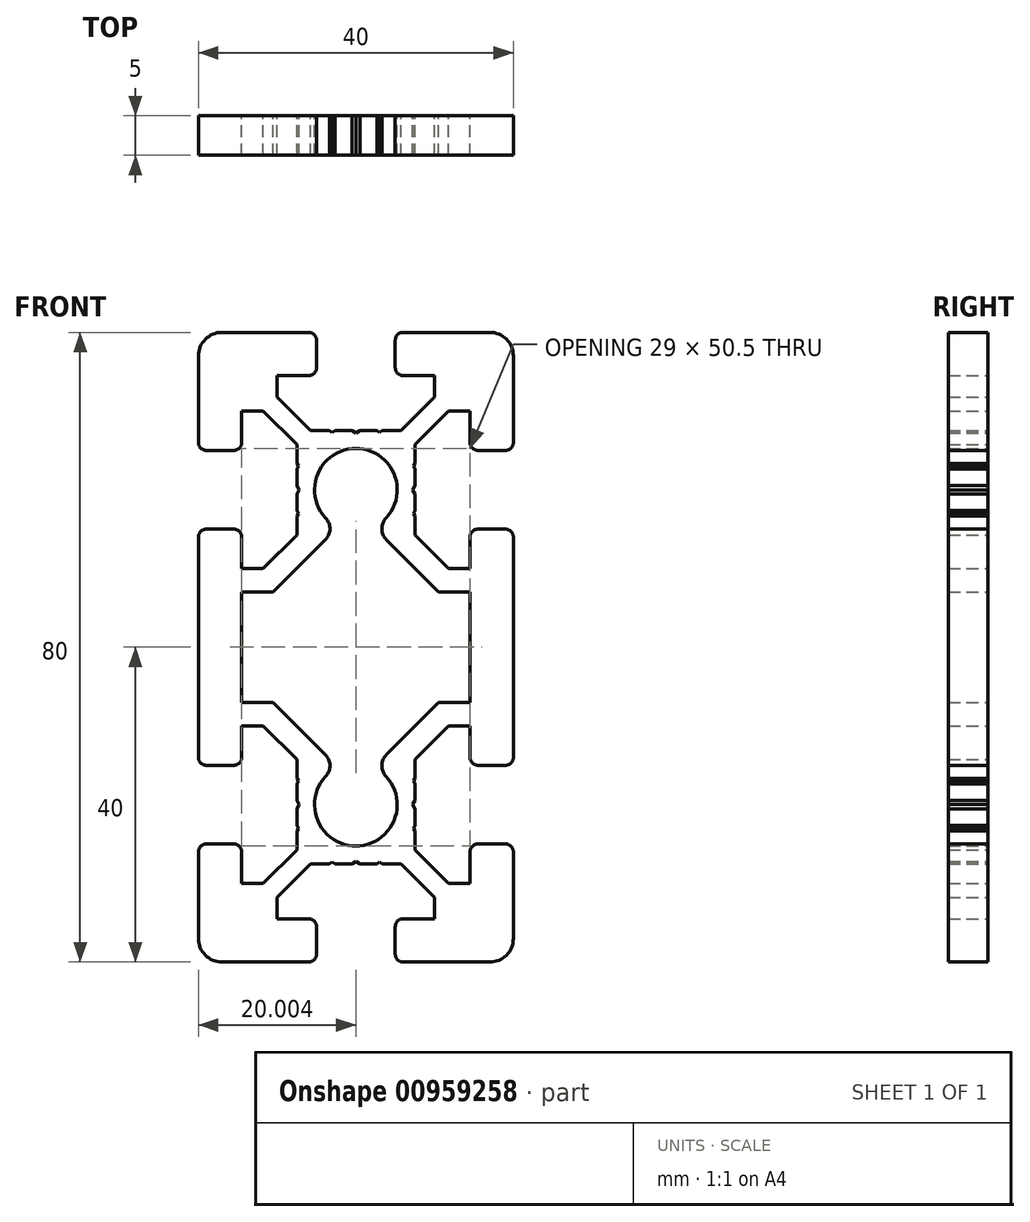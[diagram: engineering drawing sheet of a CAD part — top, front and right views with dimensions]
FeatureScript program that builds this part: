
annotation { "Feature Type Name" : "Feature", "Feature Type Description" : "" }
export const myFeature = defineFeature(function(context is Context, id is Id, definition is map)
    precondition{}
    {
        {
            assignVariable(context, id + "F0", {"name" : "length", "anyValue" : 5});
        }
        {
            var Q0;
            Q0=qCreatedBy(makeId("Front.planeOp"),FACE);
            var sketch = newSketch(context, id + "F1", { "sketchPlane" : qUnion([Q0])});
            skLineSegment(sketch, "E0", {"start": v(-9.74, 19.75) * mm, "end": v(1.29, 19.75) * mm});
            skLineSegment(sketch, "E1", {"start": v(-4.23, 14.24) * mm, "end": v(-4.23, 25.26) * mm});
            skLineSegment(sketch, "E2", {"start": v(-9.74, -20.25) * mm, "end": v(1.29, -20.25) * mm});
            skLineSegment(sketch, "E3", {"start": v(-4.23, -25.76) * mm, "end": v(-4.23, -14.74) * mm});
            skArc(sketch, "E4", {"start": v(-23.23, -25.25) * mm, "mid": v(-23.93, -25.54) * mm, "end": v(-24.23, -26.25) * mm});
            skLineSegment(sketch, "E5", {"start": v(-24.23, -26.25) * mm, "end": v(-24.23, -37.25) * mm});
            skArc(sketch, "E6", {"start": v(-24.23, -37.25) * mm, "mid": v(-23.35, -39.37) * mm, "end": v(-21.23, -40.25) * mm});
            skLineSegment(sketch, "E7", {"start": v(-21.23, -40.25) * mm, "end": v(-10.23, -40.25) * mm});
            skArc(sketch, "E8", {"start": v(-10.23, -40.25) * mm, "mid": v(-9.52, -39.96) * mm, "end": v(-9.23, -39.25) * mm});
            skLineSegment(sketch, "E9", {"start": v(-9.23, -39.25) * mm, "end": v(-9.23, -35.75) * mm});
            skArc(sketch, "E10", {"start": v(-9.23, -35.75) * mm, "mid": v(-9.52, -35.04) * mm, "end": v(-10.23, -34.75) * mm});
            skLineSegment(sketch, "E11", {"start": v(-10.23, -34.75) * mm, "end": v(-14.23, -34.75) * mm});
            skLineSegment(sketch, "E12", {"start": v(-14.23, -34.75) * mm, "end": v(-14.23, -32.02) * mm});
            skLineSegment(sketch, "E13", {"start": v(-14.23, -32.02) * mm, "end": v(-9.96, -27.75) * mm});
            skLineSegment(sketch, "E14", {"start": v(-9.96, -27.75) * mm, "end": v(-7.57, -27.75) * mm});
            skLineSegment(sketch, "E15", {"start": v(-7.57, -27.75) * mm, "end": v(-7.23, -27.55) * mm});
            skLineSegment(sketch, "E16", {"start": v(-7.23, -27.55) * mm, "end": v(-6.88, -27.75) * mm});
            skLineSegment(sketch, "E17", {"start": v(-6.88, -27.75) * mm, "end": v(-4.75, -27.75) * mm});
            skLineSegment(sketch, "E18", {"start": v(-4.75, -27.75) * mm, "end": v(-4.23, -27.45) * mm});
            skLineSegment(sketch, "E19", {"start": v(-4.23, -27.45) * mm, "end": v(-3.7, -27.75) * mm});
            skLineSegment(sketch, "E20", {"start": v(-3.7, -27.75) * mm, "end": v(-1.57, -27.75) * mm});
            skLineSegment(sketch, "E21", {"start": v(-1.57, -27.75) * mm, "end": v(-1.23, -27.55) * mm});
            skLineSegment(sketch, "E22", {"start": v(-1.23, -27.55) * mm, "end": v(-0.88, -27.75) * mm});
            skLineSegment(sketch, "E23", {"start": v(-0.88, -27.75) * mm, "end": v(1.5, -27.75) * mm});
            skLineSegment(sketch, "E24", {"start": v(1.5, -27.75) * mm, "end": v(5.77, -32.02) * mm});
            skLineSegment(sketch, "E25", {"start": v(5.77, -32.02) * mm, "end": v(5.77, -34.75) * mm});
            skLineSegment(sketch, "E26", {"start": v(5.77, -34.75) * mm, "end": v(1.77, -34.75) * mm});
            skArc(sketch, "E27", {"start": v(1.77, -34.75) * mm, "mid": v(1.07, -35.04) * mm, "end": v(0.77, -35.75) * mm});
            skLineSegment(sketch, "E28", {"start": v(0.77, -35.75) * mm, "end": v(0.77, -39.25) * mm});
            skArc(sketch, "E29", {"start": v(0.77, -39.25) * mm, "mid": v(1.07, -39.96) * mm, "end": v(1.77, -40.25) * mm});
            skLineSegment(sketch, "E30", {"start": v(1.77, -40.25) * mm, "end": v(12.77, -40.25) * mm});
            skArc(sketch, "E31", {"start": v(12.77, -40.25) * mm, "mid": v(14.9, -39.37) * mm, "end": v(15.77, -37.25) * mm});
            skLineSegment(sketch, "E32", {"start": v(15.77, -37.25) * mm, "end": v(15.77, -26.25) * mm});
            skArc(sketch, "E33", {"start": v(15.77, -26.25) * mm, "mid": v(15.48, -25.54) * mm, "end": v(14.77, -25.25) * mm});
            skLineSegment(sketch, "E34", {"start": v(14.77, -25.25) * mm, "end": v(11.27, -25.25) * mm});
            skArc(sketch, "E35", {"start": v(11.27, -25.25) * mm, "mid": v(10.57, -25.54) * mm, "end": v(10.27, -26.25) * mm});
            skLineSegment(sketch, "E36", {"start": v(10.27, -26.25) * mm, "end": v(10.27, -30.25) * mm});
            skLineSegment(sketch, "E37", {"start": v(10.27, -30.25) * mm, "end": v(7.54, -30.25) * mm});
            skLineSegment(sketch, "E38", {"start": v(7.54, -30.25) * mm, "end": v(3.27, -25.98) * mm});
            skLineSegment(sketch, "E39", {"start": v(3.27, -25.98) * mm, "end": v(3.27, -23.6) * mm});
            skLineSegment(sketch, "E40", {"start": v(3.27, -23.6) * mm, "end": v(3.07, -23.25) * mm});
            skLineSegment(sketch, "E41", {"start": v(3.07, -23.25) * mm, "end": v(3.27, -22.9) * mm});
            skLineSegment(sketch, "E42", {"start": v(3.27, -22.9) * mm, "end": v(3.27, -20.77) * mm});
            skLineSegment(sketch, "E43", {"start": v(3.27, -20.77) * mm, "end": v(2.97, -20.25) * mm});
            skLineSegment(sketch, "E44", {"start": v(2.97, -20.25) * mm, "end": v(3.27, -19.73) * mm});
            skLineSegment(sketch, "E45", {"start": v(3.27, -19.73) * mm, "end": v(3.27, -17.6) * mm});
            skLineSegment(sketch, "E46", {"start": v(3.27, -17.6) * mm, "end": v(3.07, -17.25) * mm});
            skLineSegment(sketch, "E47", {"start": v(3.07, -17.25) * mm, "end": v(3.27, -16.9) * mm});
            skLineSegment(sketch, "E48", {"start": v(3.27, -16.9) * mm, "end": v(3.27, -14.52) * mm});
            skLineSegment(sketch, "E49", {"start": v(3.27, -14.52) * mm, "end": v(7.54, -10.25) * mm});
            skLineSegment(sketch, "E50", {"start": v(7.54, -10.25) * mm, "end": v(10.27, -10.25) * mm});
            skLineSegment(sketch, "E51", {"start": v(10.27, -10.25) * mm, "end": v(10.27, -14.25) * mm});
            skArc(sketch, "E52", {"start": v(10.27, -14.25) * mm, "mid": v(10.57, -14.96) * mm, "end": v(11.27, -15.25) * mm});
            skLineSegment(sketch, "E53", {"start": v(11.27, -15.25) * mm, "end": v(14.77, -15.25) * mm});
            skArc(sketch, "E54", {"start": v(14.77, -15.25) * mm, "mid": v(15.48, -14.96) * mm, "end": v(15.77, -14.25) * mm});
            skLineSegment(sketch, "E55", {"start": v(15.77, -14.25) * mm, "end": v(15.77, 13.75) * mm});
            skArc(sketch, "E56", {"start": v(15.77, 13.75) * mm, "mid": v(15.48, 14.46) * mm, "end": v(14.77, 14.75) * mm});
            skLineSegment(sketch, "E57", {"start": v(14.77, 14.75) * mm, "end": v(11.27, 14.75) * mm});
            skArc(sketch, "E58", {"start": v(11.27, 14.75) * mm, "mid": v(10.57, 14.46) * mm, "end": v(10.27, 13.75) * mm});
            skLineSegment(sketch, "E59", {"start": v(10.27, 13.75) * mm, "end": v(10.27, 9.75) * mm});
            skLineSegment(sketch, "E60", {"start": v(10.27, 9.75) * mm, "end": v(7.54, 9.75) * mm});
            skLineSegment(sketch, "E61", {"start": v(7.54, 9.75) * mm, "end": v(3.27, 14.02) * mm});
            skLineSegment(sketch, "E62", {"start": v(3.27, 14.02) * mm, "end": v(3.27, 16.4) * mm});
            skLineSegment(sketch, "E63", {"start": v(3.27, 16.4) * mm, "end": v(3.07, 16.75) * mm});
            skLineSegment(sketch, "E64", {"start": v(3.07, 16.75) * mm, "end": v(3.27, 17.1) * mm});
            skLineSegment(sketch, "E65", {"start": v(3.27, 17.1) * mm, "end": v(3.27, 19.23) * mm});
            skLineSegment(sketch, "E66", {"start": v(3.27, 19.23) * mm, "end": v(2.97, 19.75) * mm});
            skLineSegment(sketch, "E67", {"start": v(2.97, 19.75) * mm, "end": v(3.27, 20.27) * mm});
            skLineSegment(sketch, "E68", {"start": v(3.27, 20.27) * mm, "end": v(3.27, 22.4) * mm});
            skLineSegment(sketch, "E69", {"start": v(3.27, 22.4) * mm, "end": v(3.07, 22.75) * mm});
            skLineSegment(sketch, "E70", {"start": v(3.07, 22.75) * mm, "end": v(3.27, 23.1) * mm});
            skLineSegment(sketch, "E71", {"start": v(3.27, 23.1) * mm, "end": v(3.27, 25.48) * mm});
            skLineSegment(sketch, "E72", {"start": v(3.27, 25.48) * mm, "end": v(7.54, 29.75) * mm});
            skLineSegment(sketch, "E73", {"start": v(7.54, 29.75) * mm, "end": v(10.27, 29.75) * mm});
            skLineSegment(sketch, "E74", {"start": v(10.27, 29.75) * mm, "end": v(10.27, 25.75) * mm});
            skArc(sketch, "E75", {"start": v(10.27, 25.75) * mm, "mid": v(10.57, 25.04) * mm, "end": v(11.27, 24.75) * mm});
            skLineSegment(sketch, "E76", {"start": v(11.27, 24.75) * mm, "end": v(14.77, 24.75) * mm});
            skArc(sketch, "E77", {"start": v(14.77, 24.75) * mm, "mid": v(15.48, 25.04) * mm, "end": v(15.77, 25.75) * mm});
            skLineSegment(sketch, "E78", {"start": v(15.77, 25.75) * mm, "end": v(15.77, 36.75) * mm});
            skArc(sketch, "E79", {"start": v(15.77, 36.75) * mm, "mid": v(14.9, 38.87) * mm, "end": v(12.77, 39.75) * mm});
            skLineSegment(sketch, "E80", {"start": v(12.77, 39.75) * mm, "end": v(1.77, 39.75) * mm});
            skArc(sketch, "E81", {"start": v(1.77, 39.75) * mm, "mid": v(1.07, 39.46) * mm, "end": v(0.77, 38.75) * mm});
            skLineSegment(sketch, "E82", {"start": v(0.77, 38.75) * mm, "end": v(0.77, 35.25) * mm});
            skArc(sketch, "E83", {"start": v(0.77, 35.25) * mm, "mid": v(1.07, 34.54) * mm, "end": v(1.77, 34.25) * mm});
            skLineSegment(sketch, "E84", {"start": v(1.77, 34.25) * mm, "end": v(5.77, 34.25) * mm});
            skLineSegment(sketch, "E85", {"start": v(5.77, 34.25) * mm, "end": v(5.77, 31.52) * mm});
            skLineSegment(sketch, "E86", {"start": v(5.77, 31.52) * mm, "end": v(1.5, 27.25) * mm});
            skLineSegment(sketch, "E87", {"start": v(1.5, 27.25) * mm, "end": v(-0.88, 27.25) * mm});
            skLineSegment(sketch, "E88", {"start": v(-0.88, 27.25) * mm, "end": v(-1.23, 27.05) * mm});
            skLineSegment(sketch, "E89", {"start": v(-1.23, 27.05) * mm, "end": v(-1.57, 27.25) * mm});
            skLineSegment(sketch, "E90", {"start": v(-1.57, 27.25) * mm, "end": v(-3.7, 27.25) * mm});
            skLineSegment(sketch, "E91", {"start": v(-3.7, 27.25) * mm, "end": v(-4.23, 26.95) * mm});
            skLineSegment(sketch, "E92", {"start": v(-4.23, 26.95) * mm, "end": v(-4.75, 27.25) * mm});
            skLineSegment(sketch, "E93", {"start": v(-4.75, 27.25) * mm, "end": v(-6.88, 27.25) * mm});
            skLineSegment(sketch, "E94", {"start": v(-6.88, 27.25) * mm, "end": v(-7.23, 27.05) * mm});
            skLineSegment(sketch, "E95", {"start": v(-7.23, 27.05) * mm, "end": v(-7.57, 27.25) * mm});
            skLineSegment(sketch, "E96", {"start": v(-7.57, 27.25) * mm, "end": v(-9.96, 27.25) * mm});
            skLineSegment(sketch, "E97", {"start": v(-9.96, 27.25) * mm, "end": v(-14.23, 31.52) * mm});
            skLineSegment(sketch, "E98", {"start": v(-14.23, 31.52) * mm, "end": v(-14.23, 34.25) * mm});
            skLineSegment(sketch, "E99", {"start": v(-14.23, 34.25) * mm, "end": v(-10.23, 34.25) * mm});
            skArc(sketch, "E100", {"start": v(-10.23, 34.25) * mm, "mid": v(-9.52, 34.54) * mm, "end": v(-9.23, 35.25) * mm});
            skLineSegment(sketch, "E101", {"start": v(-9.23, 35.25) * mm, "end": v(-9.23, 38.75) * mm});
            skArc(sketch, "E102", {"start": v(-9.23, 38.75) * mm, "mid": v(-9.52, 39.46) * mm, "end": v(-10.23, 39.75) * mm});
            skLineSegment(sketch, "E103", {"start": v(-10.23, 39.75) * mm, "end": v(-21.23, 39.75) * mm});
            skArc(sketch, "E104", {"start": v(-21.23, 39.75) * mm, "mid": v(-23.35, 38.87) * mm, "end": v(-24.23, 36.75) * mm});
            skLineSegment(sketch, "E105", {"start": v(-24.23, 36.75) * mm, "end": v(-24.23, 25.75) * mm});
            skArc(sketch, "E106", {"start": v(-24.23, 25.75) * mm, "mid": v(-23.93, 25.04) * mm, "end": v(-23.23, 24.75) * mm});
            skLineSegment(sketch, "E107", {"start": v(-23.23, 24.75) * mm, "end": v(-19.73, 24.75) * mm});
            skArc(sketch, "E108", {"start": v(-19.73, 24.75) * mm, "mid": v(-19.02, 25.04) * mm, "end": v(-18.73, 25.75) * mm});
            skLineSegment(sketch, "E109", {"start": v(-18.73, 25.75) * mm, "end": v(-18.73, 29.75) * mm});
            skLineSegment(sketch, "E110", {"start": v(-18.73, 29.75) * mm, "end": v(-16, 29.75) * mm});
            skLineSegment(sketch, "E111", {"start": v(-16, 29.75) * mm, "end": v(-11.73, 25.48) * mm});
            skLineSegment(sketch, "E112", {"start": v(-11.73, 25.48) * mm, "end": v(-11.73, 23.1) * mm});
            skLineSegment(sketch, "E113", {"start": v(-11.73, 23.1) * mm, "end": v(-11.53, 22.75) * mm});
            skLineSegment(sketch, "E114", {"start": v(-11.53, 22.75) * mm, "end": v(-11.73, 22.4) * mm});
            skLineSegment(sketch, "E115", {"start": v(-11.73, 22.4) * mm, "end": v(-11.73, 20.27) * mm});
            skLineSegment(sketch, "E116", {"start": v(-11.73, 20.27) * mm, "end": v(-11.43, 19.75) * mm});
            skLineSegment(sketch, "E117", {"start": v(-11.43, 19.75) * mm, "end": v(-11.73, 19.23) * mm});
            skLineSegment(sketch, "E118", {"start": v(-11.73, 19.23) * mm, "end": v(-11.73, 17.1) * mm});
            skLineSegment(sketch, "E119", {"start": v(-11.73, 17.1) * mm, "end": v(-11.53, 16.75) * mm});
            skLineSegment(sketch, "E120", {"start": v(-11.53, 16.75) * mm, "end": v(-11.73, 16.4) * mm});
            skLineSegment(sketch, "E121", {"start": v(-11.73, 16.4) * mm, "end": v(-11.73, 14.02) * mm});
            skLineSegment(sketch, "E122", {"start": v(-11.73, 14.02) * mm, "end": v(-16, 9.75) * mm});
            skLineSegment(sketch, "E123", {"start": v(-16, 9.75) * mm, "end": v(-18.73, 9.75) * mm});
            skLineSegment(sketch, "E124", {"start": v(-18.73, 9.75) * mm, "end": v(-18.73, 13.75) * mm});
            skArc(sketch, "E125", {"start": v(-18.73, 13.75) * mm, "mid": v(-19.02, 14.46) * mm, "end": v(-19.73, 14.75) * mm});
            skLineSegment(sketch, "E126", {"start": v(-19.73, 14.75) * mm, "end": v(-23.23, 14.75) * mm});
            skArc(sketch, "E127", {"start": v(-23.23, 14.75) * mm, "mid": v(-23.93, 14.46) * mm, "end": v(-24.23, 13.75) * mm});
            skLineSegment(sketch, "E128", {"start": v(-24.23, 13.75) * mm, "end": v(-24.23, -14.25) * mm});
            skArc(sketch, "E129", {"start": v(-24.23, -14.25) * mm, "mid": v(-23.93, -14.96) * mm, "end": v(-23.23, -15.25) * mm});
            skLineSegment(sketch, "E130", {"start": v(-23.23, -15.25) * mm, "end": v(-19.73, -15.25) * mm});
            skArc(sketch, "E131", {"start": v(-19.73, -15.25) * mm, "mid": v(-19.02, -14.96) * mm, "end": v(-18.73, -14.25) * mm});
            skLineSegment(sketch, "E132", {"start": v(-18.73, -14.25) * mm, "end": v(-18.73, -10.25) * mm});
            skLineSegment(sketch, "E133", {"start": v(-18.73, -10.25) * mm, "end": v(-16, -10.25) * mm});
            skLineSegment(sketch, "E134", {"start": v(-16, -10.25) * mm, "end": v(-11.73, -14.52) * mm});
            skLineSegment(sketch, "E135", {"start": v(-11.73, -14.52) * mm, "end": v(-11.73, -16.9) * mm});
            skLineSegment(sketch, "E136", {"start": v(-11.73, -16.9) * mm, "end": v(-11.53, -17.25) * mm});
            skLineSegment(sketch, "E137", {"start": v(-11.53, -17.25) * mm, "end": v(-11.73, -17.6) * mm});
            skLineSegment(sketch, "E138", {"start": v(-11.73, -17.6) * mm, "end": v(-11.73, -19.73) * mm});
            skLineSegment(sketch, "E139", {"start": v(-11.73, -19.73) * mm, "end": v(-11.43, -20.25) * mm});
            skLineSegment(sketch, "E140", {"start": v(-11.43, -20.25) * mm, "end": v(-11.73, -20.77) * mm});
            skLineSegment(sketch, "E141", {"start": v(-11.73, -20.77) * mm, "end": v(-11.73, -22.9) * mm});
            skLineSegment(sketch, "E142", {"start": v(-11.73, -22.9) * mm, "end": v(-11.53, -23.25) * mm});
            skLineSegment(sketch, "E143", {"start": v(-11.53, -23.25) * mm, "end": v(-11.73, -23.6) * mm});
            skLineSegment(sketch, "E144", {"start": v(-11.73, -23.6) * mm, "end": v(-11.73, -25.98) * mm});
            skLineSegment(sketch, "E145", {"start": v(-11.73, -25.98) * mm, "end": v(-16, -30.25) * mm});
            skLineSegment(sketch, "E146", {"start": v(-16, -30.25) * mm, "end": v(-18.73, -30.25) * mm});
            skLineSegment(sketch, "E147", {"start": v(-18.73, -30.25) * mm, "end": v(-18.73, -26.25) * mm});
            skArc(sketch, "E148", {"start": v(-18.73, -26.25) * mm, "mid": v(-19.02, -25.54) * mm, "end": v(-19.73, -25.25) * mm});
            skLineSegment(sketch, "E149", {"start": v(-18.73, 6.75) * mm, "end": v(-18.73, -7.25) * mm});
            skLineSegment(sketch, "E150", {"start": v(-14.75, 6.75) * mm, "end": v(-18.73, 6.75) * mm});
            skLineSegment(sketch, "E151", {"start": v(-8.11, 13.39) * mm, "end": v(-14.75, 6.75) * mm});
            skArc(sketch, "E152", {"start": v(-8.11, 13.39) * mm, "mid": v(-7.53, 14.77) * mm, "end": v(-8.06, 16.17) * mm});
            skArc(sketch, "E153", {"start": v(-0.39, 16.17) * mm, "mid": v(-4.23, 25) * mm, "end": v(-8.06, 16.17) * mm});
            skArc(sketch, "E154", {"start": v(-0.39, 16.17) * mm, "mid": v(-0.93, 14.77) * mm, "end": v(-0.34, 13.39) * mm});
            skLineSegment(sketch, "E155", {"start": v(6.3, 6.75) * mm, "end": v(-0.34, 13.39) * mm});
            skLineSegment(sketch, "E156", {"start": v(10.27, 6.75) * mm, "end": v(6.3, 6.75) * mm});
            skLineSegment(sketch, "E157", {"start": v(10.27, -7.25) * mm, "end": v(10.27, 6.75) * mm});
            skLineSegment(sketch, "E158", {"start": v(6.3, -7.25) * mm, "end": v(10.27, -7.25) * mm});
            skLineSegment(sketch, "E159", {"start": v(-0.34, -13.89) * mm, "end": v(6.3, -7.25) * mm});
            skArc(sketch, "E160", {"start": v(-0.34, -13.89) * mm, "mid": v(-0.93, -15.27) * mm, "end": v(-0.39, -16.67) * mm});
            skArc(sketch, "E161", {"start": v(-8.06, -16.67) * mm, "mid": v(-4.23, -25.5) * mm, "end": v(-0.39, -16.67) * mm});
            skArc(sketch, "E162", {"start": v(-8.06, -16.67) * mm, "mid": v(-7.53, -15.27) * mm, "end": v(-8.11, -13.89) * mm});
            skLineSegment(sketch, "E163", {"start": v(-14.75, -7.25) * mm, "end": v(-8.11, -13.89) * mm});
            skLineSegment(sketch, "E164", {"start": v(-18.73, -7.25) * mm, "end": v(-14.75, -7.25) * mm});
            skLineSegment(sketch, "E165", {"start": v(-19.73, -25.25) * mm, "end": v(-23.23, -25.25) * mm});
            skSolve(sketch);
        }
        {
            var Q0;
            Q0=makeQuery(id+"F1.imprint","IMPRINT",FACE,{"disambiguationData":[TD([[makeQuery(id+"F1.imprint","IMPRINT",EDGE,{"derivedFrom":sQuery(id+"F1.wireOp",EDGE,"E4")}),1.0]])]});
            extrude(context, id + "F2", {"entities" : qUnion([Q0]), "depth" : (getVariable(context, 'length')) * mm, "offsetDistance" : 25 * mm});
        }
    });
